# Revit family: Trap-BidetTrap-PType-Vitra-Other-A45118
name_source: partatom
category: Plumbing Fixtures
revit_build: Autodesk Revit 2017 (Build: 20160225_1515(x64)
units: mm (PartAtom-declared; Revit-internal decimal feet)

## family parameters
Always vertical = No
Cut with Voids When Loaded = No
OmniClass Number = 23.45.00.00
OmniClass Title = Sanitary, Laundry, and Cleaning Equipment
Part Type = Normal
Room Calculation Point = No
Round Connector Dimension = Use Diameter
Shared = No
Work Plane-Based = Yes

## types (5) — shared parameters
BIMobject category = Sanitary - Taps & Mixers
Brand = VitrA
CW Connection = Yes
Coating Material = Chrome
Connection Diameter (mm) = 15 mm  [stored 0.0492126 ft]
Date of publishing = 2003
Default Elevation = 650 mm  [stored 2.13255 ft]
Depth(mm) = 355 mm
Description = Traps Bidet Trap (P Type)
HW Connection = Yes
Height(mm) = 110 mm  [stored 0.360892 ft]
IFC Classification = Sanitary Terminal
Manufacturer = Vitra
Manufacturer country = Turkey
Manufacturer name = Vitra
Masterformat 2014 Code = 22 40 00
Masterformat 2014 Description = Plumbing Fixtures
MountingType = Pipe connection
NBS Reference Code = 401425
NBS Reference Description = Traps and strainers
Number Of Connections = 1
OmniClass Code = 23-27 37 00
OmniClass Description = Liquid Traps
Product Type = Trap
Product certification = https://vitraglobal.com
Product data url = https://www.vitraglobal.com
Product family = OtherSeries
Product group = P Type Trap
Technical description = https://www.vitraglobal.com
UNSPSC Code = 401425
UNSPSC Description = Traps and strainers
URL = https://vitraglobal.com
Uniclass 1.4 Code = L7218
Uniclass 1.4 Description = Traps for sinks and basins
Uniclass 2.0 Code = PR-62-24
Uniclass 2.0 Description = Drainage Traps
Uniclass 2015 Code = Pr_65_52_25
Uniclass 2015 Name = Drainage traps and accessories
Uniformat II Code = D2010
Uniformat II Description = Plumbing Fixtures
Warranty Period (Year) = 5
Weight Net (Kg) = 0.908
Width(mm) = 70 mm  [stored 0.229659 ft]
Youtube clip = https://www.youtube.com
zero-valued in all types: Cost, Nominal height, Nominal width

## per-type parameters (varying)
| type | Article No. (default) | Color | Model | Product SKU |
| Trap-BidetTrap-PType-Vitra-Other-A45118 | A45118 | Chrome | A45118 | A45118 |
| Trap-BidetTrap-PType-Vitra-Other-A4511823EXP | A4511823EXP |  | A4511823EXP | A4511823EXP |
| Trap-BidetTrap-PType-Vitra-Other-A45118EXP | A45118EXP | Chrome | A45118EXP | A45118EXP |
| Trap-BidetTrap-PType-Vitra-Other-A45118TPL | A45118TPL | Chrome | A45118TPL | A45118TPL |
| Trap-BidetTrap-PType-Vitra-Other-A45118TPX | A45118TPX | Chrome | A45118TPX | A45118TPX |

note: [stored X ft] marks values corroborated as IEEE doubles in the binary element streams (Revit-internal decimal feet)

## geometry (parser evidence)
native form markers: Sweep x2
no freeform markers — native parametric forms only
